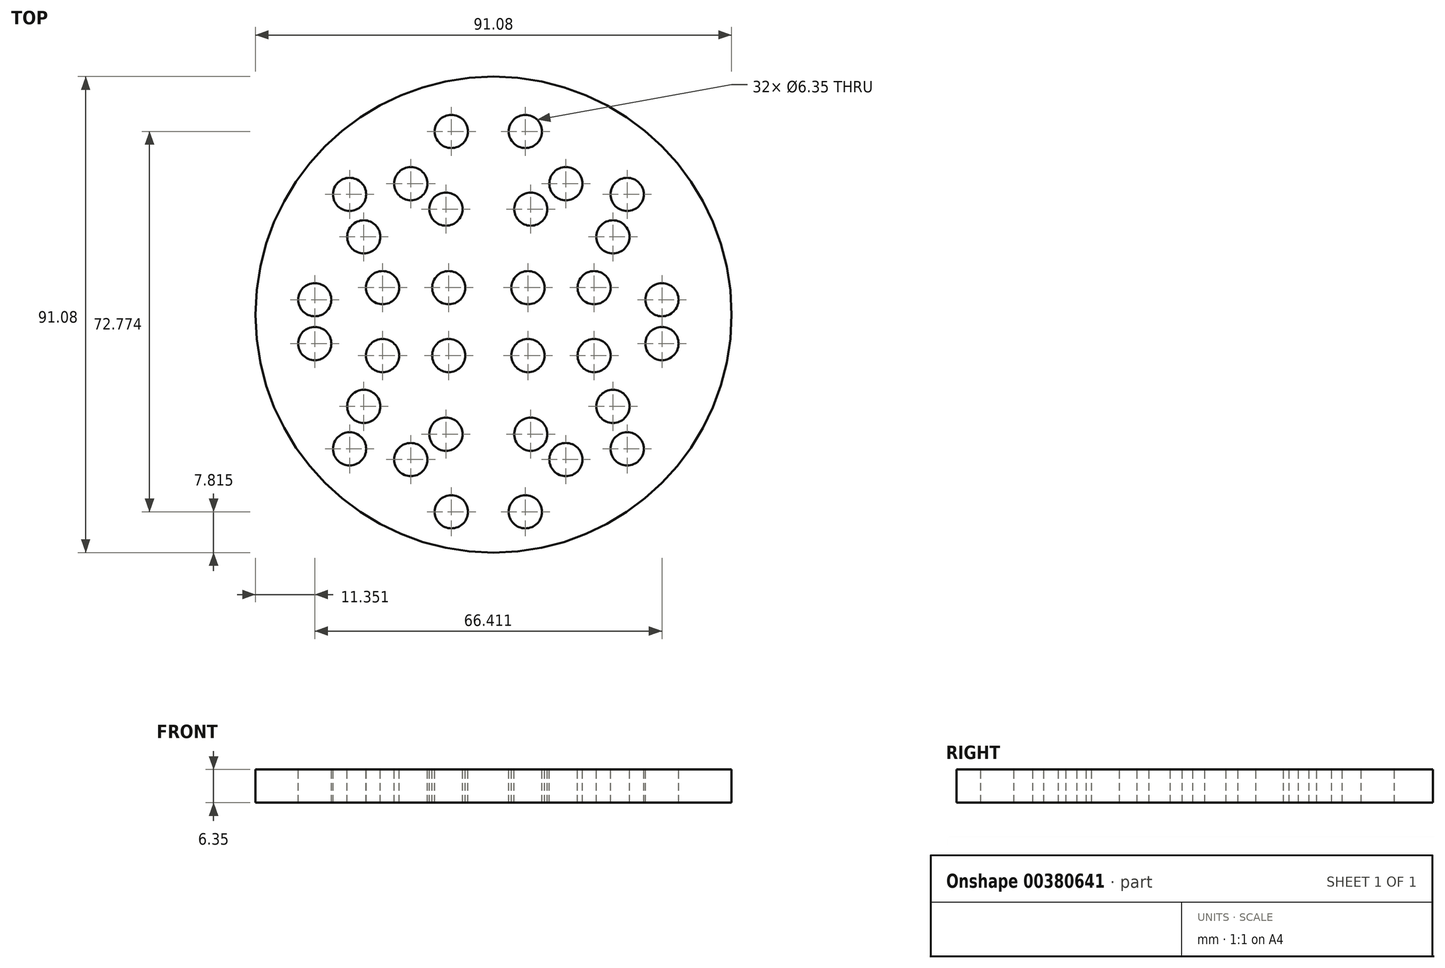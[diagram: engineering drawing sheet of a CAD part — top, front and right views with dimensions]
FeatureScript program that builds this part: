
annotation { "Feature Type Name" : "Feature", "Feature Type Description" : "" }
export const myFeature = defineFeature(function(context is Context, id is Id, definition is map)
    precondition{}
    {
        {
            var Q0;
            Q0=qCreatedBy(makeId("Top.planeOp"),FACE);
            var sketch = newSketch(context, id + "F0", { "sketchPlane" : qUnion([Q0])});
            skCircle(sketch, "E0", {"center": v(0, 0) * mm, "radius": 45.54 * mm});
            skSolve(sketch);
        }
        {
            var Q0;
            Q0=qCreatedBy(makeId("Top.planeOp"),FACE);
            var sketch = newSketch(context, id + "F1", { "sketchPlane" : qUnion([Q0])});
            skLineSegment(sketch, "E1", {"start": v(-0.98, -41.8) * mm, "end": v(-0.98, 39.13) * mm});
            skLineSegment(sketch, "E2", {"start": v(-0.98, -1.34) * mm, "end": v(39.48, -1.34) * mm});
            skLineSegment(sketch, "E3", {"start": v(39.48, -1.34) * mm, "end": v(-0.98, -1.34) * mm});
            skLineSegment(sketch, "E4", {"start": v(-0.98, -1.34) * mm, "end": v(-41.45, -1.34) * mm});
            skPoint(sketch, "E5", {"position": v(-8.06, 35.05) * mm});
            skPoint(sketch, "E6", {"position": v(-27.53, 23) * mm});
            skPoint(sketch, "E7", {"position": v(-34.19, 2.86) * mm});
            skPoint(sketch, "E8", {"position": v(-9.1, 20.2) * mm});
            skPoint(sketch, "E9", {"position": v(-21.22, 5.16) * mm});
            skPoint(sketch, "E10", {"position": v(-8.57, 5.16) * mm});
            skPoint(sketch, "E11", {"position": v(-21.22, -1.34) * mm});
            skPoint(sketch, "E12", {"position": v(-24.8, 14.88) * mm});
            skPoint(sketch, "E13", {"position": v(-15.82, 25.06) * mm});
            skLineSegment(sketch, "E14.MirrorCS", {"start": v(-41.45, -1.34) * mm, "end": v(-0.98, -1.34) * mm});
            skPoint(sketch, "E15.MirrorP", {"position": v(6.6, 5.16) * mm});
            skPoint(sketch, "E16.MirrorP", {"position": v(7.14, 20.2) * mm});
            skPoint(sketch, "E17.MirrorP", {"position": v(19.25, 5.16) * mm});
            skPoint(sketch, "E18.MirrorP", {"position": v(32.22, 2.86) * mm});
            skPoint(sketch, "E19.MirrorP", {"position": v(25.57, 23) * mm});
            skPoint(sketch, "E20.MirrorP", {"position": v(22.84, 14.88) * mm});
            skPoint(sketch, "E21.MirrorP", {"position": v(13.85, 25.06) * mm});
            skPoint(sketch, "E22.MirrorP", {"position": v(6.1, 35.05) * mm});
            skPoint(sketch, "E23.MirrorP", {"position": v(6.6, -7.83) * mm});
            skPoint(sketch, "E24.MirrorP", {"position": v(19.25, -7.83) * mm});
            skPoint(sketch, "E25.MirrorP", {"position": v(32.22, -5.53) * mm});
            skPoint(sketch, "E26.MirrorP", {"position": v(22.84, -17.55) * mm});
            skPoint(sketch, "E27.MirrorP", {"position": v(25.57, -25.68) * mm});
            skPoint(sketch, "E28.MirrorP", {"position": v(13.85, -27.74) * mm});
            skPoint(sketch, "E29.MirrorP", {"position": v(7.14, -22.87) * mm});
            skPoint(sketch, "E30.MirrorP", {"position": v(6.1, -37.72) * mm});
            skPoint(sketch, "E31.MirrorP", {"position": v(-8.06, -37.72) * mm});
            skPoint(sketch, "E32.MirrorP", {"position": v(-15.82, -27.74) * mm});
            skPoint(sketch, "E33.MirrorP", {"position": v(-9.1, -22.87) * mm});
            skPoint(sketch, "E34.MirrorP", {"position": v(-27.53, -25.68) * mm});
            skPoint(sketch, "E35.MirrorP", {"position": v(-24.8, -17.55) * mm});
            skPoint(sketch, "E36.MirrorP", {"position": v(-21.22, -7.83) * mm});
            skPoint(sketch, "E37.MirrorP", {"position": v(-34.19, -5.53) * mm});
            skPoint(sketch, "E38.MirrorP", {"position": v(-8.57, -7.83) * mm});
            skSolve(sketch);
        }
        {
            var Q0;
            Q0=makeQuery(id+"F0.imprint","IMPRINT",FACE,{"disambiguationData":[TD([[makeQuery(id+"F0.imprint","IMPRINT",EDGE,{"derivedFrom":sQuery(id+"F0.wireOp",EDGE,"E0")}),1.0]])]});
            var Q1;
            Q1=sQuery(id+"F0.wireOp",EDGE,"E0");
            extrude(context, id + "F2", {"entities" : qUnion([Q0]), "surfaceEntities" : qUnion([Q1]), "oppositeDirection" : true, "depth" : 6.35 * mm});
        }
        {
            var Q0;
            Q0=sQuery(id+"F1.wireOp",VERTEX,"E33.MirrorP");
            var Q1;
            Q1=sQuery(id+"F1.wireOp",VERTEX,"E32.MirrorP");
            var Q2;
            Q2=sQuery(id+"F1.wireOp",VERTEX,"E34.MirrorP");
            var Q3;
            Q3=sQuery(id+"F1.wireOp",VERTEX,"E35.MirrorP");
            var Q4;
            Q4=sQuery(id+"F1.wireOp",VERTEX,"E38.MirrorP");
            var Q5;
            Q5=sQuery(id+"F1.wireOp",VERTEX,"E36.MirrorP");
            var Q6;
            Q6=sQuery(id+"F1.wireOp",VERTEX,"E28.MirrorP");
            var Q7;
            Q7=sQuery(id+"F1.wireOp",VERTEX,"E27.MirrorP");
            var Q8;
            Q8=sQuery(id+"F1.wireOp",VERTEX,"E26.MirrorP");
            var Q9;
            Q9=sQuery(id+"F1.wireOp",VERTEX,"E29.MirrorP");
            var Q10;
            Q10=sQuery(id+"F1.wireOp",VERTEX,"E30.MirrorP");
            var Q11;
            Q11=sQuery(id+"F1.wireOp",VERTEX,"E31.MirrorP");
            var Q12;
            Q12=sQuery(id+"F1.wireOp",VERTEX,"E23.MirrorP");
            var Q13;
            Q13=sQuery(id+"F1.wireOp",VERTEX,"E24.MirrorP");
            var Q14;
            Q14=sQuery(id+"F1.wireOp",VERTEX,"E25.MirrorP");
            var Q15;
            Q15=sQuery(id+"F1.wireOp",VERTEX,"E18.MirrorP");
            var Q16;
            Q16=sQuery(id+"F1.wireOp",VERTEX,"E17.MirrorP");
            var Q17;
            Q17=sQuery(id+"F1.wireOp",VERTEX,"E15.MirrorP");
            var Q18;
            Q18=sQuery(id+"F1.wireOp",VERTEX,"E16.MirrorP");
            var Q19;
            Q19=sQuery(id+"F1.wireOp",VERTEX,"E21.MirrorP");
            var Q20;
            Q20=sQuery(id+"F1.wireOp",VERTEX,"E19.MirrorP");
            var Q21;
            Q21=sQuery(id+"F1.wireOp",VERTEX,"E20.MirrorP");
            var Q22;
            Q22=sQuery(id+"F1.wireOp",VERTEX,"E22.MirrorP");
            var Q23;
            Q23=sQuery(id+"F1.wireOp",VERTEX,"E10");
            var Q24;
            Q24=sQuery(id+"F1.wireOp",VERTEX,"E9");
            var Q25;
            Q25=sQuery(id+"F1.wireOp",VERTEX,"E7");
            var Q26;
            Q26=sQuery(id+"F1.wireOp",VERTEX,"E37.MirrorP");
            var Q27;
            Q27=sQuery(id+"F1.wireOp",VERTEX,"E8");
            var Q28;
            Q28=sQuery(id+"F1.wireOp",VERTEX,"E12");
            var Q29;
            Q29=sQuery(id+"F1.wireOp",VERTEX,"E13");
            var Q30;
            Q30=sQuery(id+"F1.wireOp",VERTEX,"E6");
            var Q31;
            Q31=sQuery(id+"F1.wireOp",VERTEX,"E5");
            var Q32;
            Q32=makeQuery(id+"F2.opExtrude","SWEPT_BODY",BODY,{"disambiguationData":[OSD([sQuery(id+"F0.wireOp",EDGE,"E0")])]});
            hole(context, id + "F3", {"style" : HoleStyle.SIMPLE, "endStyle" : HoleEndStyle.THROUGH, "holeDiameter" : 6.35 * mm, "isTappedThrough" : true, "tappedDepth" : 12.7 * mm, "tapClearance" : 3, "locations" : qUnion([Q0, Q1, Q2, Q3, Q4, Q5, Q6, Q7, Q8, Q9, Q10, Q11, Q12, Q13, Q14, Q15, Q16, Q17, Q18, Q19, Q20, Q21, Q22, Q23, Q24, Q25, Q26, Q27, Q28, Q29, Q30, Q31]), "scope" : qUnion([Q32])});
        }
    });
